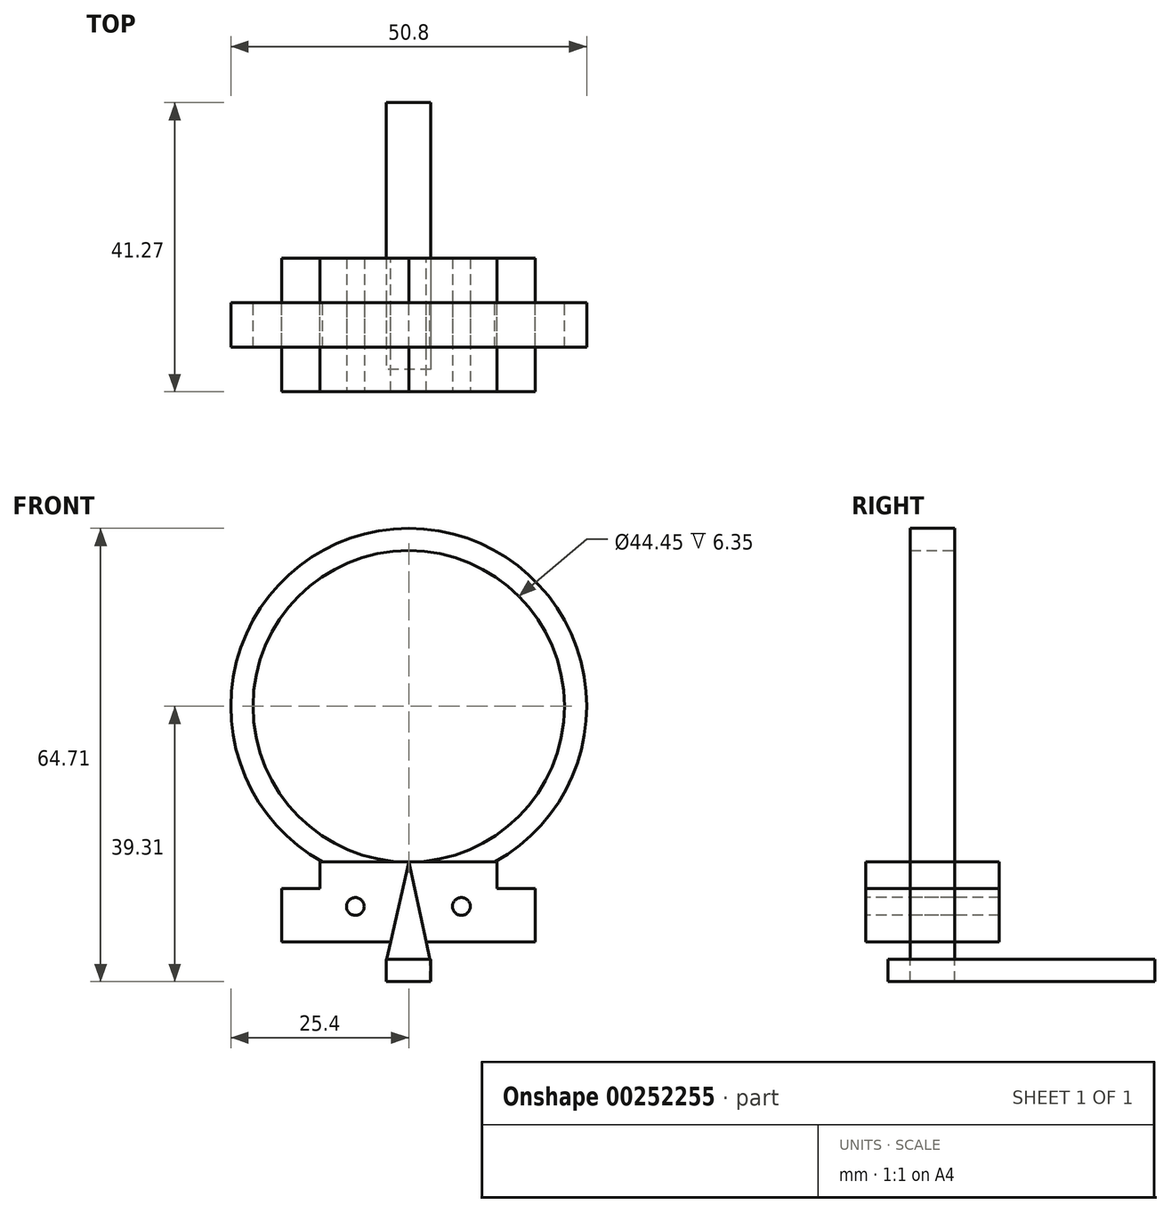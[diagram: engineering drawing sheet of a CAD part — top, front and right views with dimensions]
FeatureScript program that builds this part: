
annotation { "Feature Type Name" : "Feature", "Feature Type Description" : "" }
export const myFeature = defineFeature(function(context is Context, id is Id, definition is map)
    precondition{}
    {
        {
            var Q0;
            Q0=qCreatedBy(makeId("Front.planeOp"),FACE);
            var sketch = newSketch(context, id + "F0", { "sketchPlane" : qUnion([Q0])});
            skArc(sketch, "E0", {"start": v(0, 50.8) * mm, "mid": v(25.36, 26.9) * mm, "end": v(3, 0.18) * mm});
            skArc(sketch, "E1", {"start": v(0, 3.17) * mm, "mid": v(22.23, 25.4) * mm, "end": v(0, 47.63) * mm});
            skFitSpline(sketch, "E2", {"points": [v(0, 50.8) * mm, v(1.45, 49.21) * mm, v(0, 47.63) * mm], "startDerivative": vector(4.36, -3.17) * mm, "endDerivative": vector(-4.36, -3.17) * mm});
            skArc(sketch, "E3", {"start": v(0, 50.8) * mm, "mid": v(-25.36, 26.9) * mm, "end": v(-3, 0.18) * mm});
            skArc(sketch, "E4", {"start": v(0, 47.63) * mm, "mid": v(-22.23, 25.4) * mm, "end": v(0, 3.17) * mm});
            skLineSegment(sketch, "E5", {"start": v(-3, 0.18) * mm, "end": v(0, 3.17) * mm});
            skLineSegment(sketch, "E6", {"start": v(3, 0.18) * mm, "end": v(0, 3.17) * mm});
            skPoint(sketch, "E7.orphan", {"position": v(0, 0) * mm});
            skLineSegment(sketch, "E8", {"start": v(0, 3.17) * mm, "end": v(-12.7, 3.17) * mm});
            skLineSegment(sketch, "E9", {"start": v(-12.7, 3.17) * mm, "end": v(-12.7, -0.64) * mm});
            skLineSegment(sketch, "E10", {"start": v(12.6, -0.64) * mm, "end": v(12.6, 3.17) * mm});
            skLineSegment(sketch, "E11", {"start": v(12.6, 3.17) * mm, "end": v(0, 3.17) * mm});
            skLineSegment(sketch, "E12", {"start": v(-12.7, -0.64) * mm, "end": v(-18.16, -0.64) * mm});
            skLineSegment(sketch, "E13", {"start": v(12.6, -0.64) * mm, "end": v(18.06, -0.64) * mm});
            skLineSegment(sketch, "E14", {"start": v(-18.16, -0.64) * mm, "end": v(-18.16, -8.26) * mm});
            skLineSegment(sketch, "E15", {"start": v(-18.16, -8.26) * mm, "end": v(-2.59, -8.26) * mm});
            skLineSegment(sketch, "E16", {"start": v(18.06, -0.64) * mm, "end": v(18.06, -8.26) * mm});
            skLineSegment(sketch, "E17", {"start": v(2.5, -8.26) * mm, "end": v(0, 3.17) * mm});
            skLineSegment(sketch, "E18", {"start": v(0, 3.17) * mm, "end": v(-2.59, -8.26) * mm});
            skLineSegment(sketch, "E19", {"start": v(-2.59, -8.26) * mm, "end": v(-3.15, -10.73) * mm});
            skLineSegment(sketch, "E20", {"start": v(2.5, -8.26) * mm, "end": v(3.03, -10.74) * mm});
            skLineSegment(sketch, "E21", {"start": v(3.03, -10.74) * mm, "end": v(-3.15, -10.73) * mm});
            skLineSegment(sketch, "E22.trimOffspring", {"start": v(2.5, -8.26) * mm, "end": v(18.06, -8.26) * mm});
            skSolve(sketch);
        }
        {
            var Q0;
            {var subQ4=sQuery(id+"F0.wireOp",EDGE,"E6");Q0=makeQuery(id+"F0.imprint","IMPRINT",FACE,{"disambiguationData":[TD([[makeQuery(id+"F0.imprint","IMPRINT",EDGE,{"derivedFrom":subQ4}),1.0]])]});}
            var Q1;
            {var subQ4=sQuery(id+"F0.wireOp",EDGE,"E5");Q1=makeQuery(id+"F0.imprint","IMPRINT",FACE,{"disambiguationData":[TD([[makeQuery(id+"F0.imprint","IMPRINT",EDGE,{"derivedFrom":subQ4}),-1.0]])]});}
            var Q2;
            {var subQ0=sQuery(id+"F0.wireOp",EDGE,"E6");Q2=makeQuery(id+"F0.imprint","IMPRINT",FACE,{"disambiguationData":[TD([[makeQuery(id+"F0.imprint","IMPRINT",EDGE,{"derivedFrom":subQ0}),-1.0]])]});}
            var Q3;
            {var subQ0=sQuery(id+"F0.wireOp",EDGE,"E5");Q3=makeQuery(id+"F0.imprint","IMPRINT",FACE,{"disambiguationData":[TD([[makeQuery(id+"F0.imprint","IMPRINT",EDGE,{"derivedFrom":subQ0}),1.0]])]});}
            extrude(context, id + "F1", {"entities" : qUnion([Q0, Q1, Q2, Q3]), "depth" : 12.7 * mm});
        }
        {
            var Q0;
            Q0=makeQuery(id+"F1.opExtrude","CAP_FACE",FACE,{"disambiguationData":[OSD([sQuery(id+"F0.wireOp",EDGE,"E0"),sQuery(id+"F0.wireOp",EDGE,"E6"),sQuery(id+"F0.wireOp",EDGE,"E10"),sQuery(id+"F0.wireOp",EDGE,"E11"),sQuery(id+"F0.wireOp",EDGE,"E13"),sQuery(id+"F0.wireOp",EDGE,"E15"),sQuery(id+"F0.wireOp",EDGE,"E16"),sQuery(id+"F0.wireOp",EDGE,"E17")])],"isStart":true});
            var Q1;
            Q1=makeQuery(id+"F1.opExtrude","CAP_FACE",FACE,{"disambiguationData":[OSD([sQuery(id+"F0.wireOp",EDGE,"E3"),sQuery(id+"F0.wireOp",EDGE,"E5"),sQuery(id+"F0.wireOp",EDGE,"E8"),sQuery(id+"F0.wireOp",EDGE,"E9"),sQuery(id+"F0.wireOp",EDGE,"E12"),sQuery(id+"F0.wireOp",EDGE,"E14"),sQuery(id+"F0.wireOp",EDGE,"E15"),sQuery(id+"F0.wireOp",EDGE,"E18")])],"isStart":true});
            extrude(context, id + "F2", {"entities" : qUnion([Q0, Q1]), "operationType" : NewBodyOperationType.ADD, "depth" : 6.35 * mm});
        }
        {
            var Q0;
            Q0 = qSketchRegion(id + "F0", true);
            extrude(context, id + "F3", {"entities" : qUnion([Q0]), "depth" : 6.35 * mm});
        }
        {
            var Q0;
            Q0=makeQuery(id+"F3.opExtrude","SWEPT_FACE",FACE,{"disambiguationData":[OSD([sQuery(id+"F0.wireOp",EDGE,"E21")])]});
            var sketch = newSketch(context, id + "F4", { "sketchPlane" : qUnion([Q0])});
            skLineSegment(sketch, "E23", {"start": v(0, 0) * mm, "end": v(0, 6.35) * mm});
            skLineSegment(sketch, "E24.top", {"start": v(3.18, 9.53) * mm, "end": v(-3.17, 9.53) * mm});
            skLineSegment(sketch, "E24.left", {"start": v(3.18, -3.18) * mm, "end": v(3.18, 9.53) * mm});
            skLineSegment(sketch, "E24.right", {"start": v(-3.18, -3.18) * mm, "end": v(-3.17, 9.53) * mm});
            skPoint(sketch, "E24.middle", {"position": v(0, 3.18) * mm});
            skLineSegment(sketch, "E25", {"start": v(-3.18, -3.18) * mm, "end": v(-3.18, -28.58) * mm});
            skLineSegment(sketch, "E26", {"start": v(-3.18, -28.58) * mm, "end": v(3.18, -28.58) * mm});
            skLineSegment(sketch, "E27", {"start": v(3.18, -28.58) * mm, "end": v(3.18, -3.18) * mm});
            skSolve(sketch);
        }
        {
            var Q0;
            Q0=makeQuery(id+"F4.imprint","IMPRINT",FACE,{"disambiguationData":[TD([[makeQuery(id+"F4.imprint","IMPRINT",EDGE,{"derivedFrom":sQuery(id+"F4.wireOp",EDGE,"E24.top")}),1.0]])]});
            extrude(context, id + "F5", {"entities" : qUnion([Q0]), "operationType" : NewBodyOperationType.ADD, "depth" : 3.17 * mm});
        }
        {
            var Q0;
            Q0=makeQuery(id+"F1.opExtrude","CAP_FACE",FACE,{"disambiguationData":[OSD([sQuery(id+"F0.wireOp",EDGE,"E8"),sQuery(id+"F0.wireOp",EDGE,"E9"),sQuery(id+"F0.wireOp",EDGE,"E12"),sQuery(id+"F0.wireOp",EDGE,"E14"),sQuery(id+"F0.wireOp",EDGE,"E15"),sQuery(id+"F0.wireOp",EDGE,"E18")])],"isStart":false});
            var sketch = newSketch(context, id + "F6", { "sketchPlane" : qUnion([Q0])});
            skCircle(sketch, "E28", {"center": v(-7.62, -3.18) * mm, "radius": 1.27 * mm});
            skSolve(sketch);
        }
        {
            var Q0;
            Q0=makeQuery(id+"F1.opExtrude","CAP_FACE",FACE,{"disambiguationData":[OSD([sQuery(id+"F0.wireOp",EDGE,"E10"),sQuery(id+"F0.wireOp",EDGE,"E11"),sQuery(id+"F0.wireOp",EDGE,"E13"),sQuery(id+"F0.wireOp",EDGE,"E16"),sQuery(id+"F0.wireOp",EDGE,"E17"),sQuery(id+"F0.wireOp",EDGE,"E22.trimOffspring")])],"isStart":false});
            var sketch = newSketch(context, id + "F7", { "sketchPlane" : qUnion([Q0])});
            skCircle(sketch, "E29", {"center": v(7.52, -3.18) * mm, "radius": 1.27 * mm});
            skSolve(sketch);
        }
        {
            var Q0;
            Q0=sQuery(id+"F6.wireOp",VERTEX,"E28.center");
            var Q1;
            Q1=makeQuery(id+"F1.opExtrude","SWEPT_BODY",BODY,{"disambiguationData":[OSD([sQuery(id+"F0.wireOp",EDGE,"E8"),sQuery(id+"F0.wireOp",EDGE,"E9"),sQuery(id+"F0.wireOp",EDGE,"E12"),sQuery(id+"F0.wireOp",EDGE,"E14"),sQuery(id+"F0.wireOp",EDGE,"E15"),sQuery(id+"F0.wireOp",EDGE,"E18")])]});
            var Q2;
            Q2=makeQuery(id+"F3.opExtrude","SWEPT_BODY",BODY,{"disambiguationData":[OSD([sQuery(id+"F0.wireOp",EDGE,"E0"),sQuery(id+"F0.wireOp",EDGE,"E1"),sQuery(id+"F0.wireOp",EDGE,"E3"),sQuery(id+"F0.wireOp",EDGE,"E4"),sQuery(id+"F0.wireOp",EDGE,"E8"),sQuery(id+"F0.wireOp",EDGE,"E9"),sQuery(id+"F0.wireOp",EDGE,"E10"),sQuery(id+"F0.wireOp",EDGE,"E11"),sQuery(id+"F0.wireOp",EDGE,"E12"),sQuery(id+"F0.wireOp",EDGE,"E13"),sQuery(id+"F0.wireOp",EDGE,"E14"),sQuery(id+"F0.wireOp",EDGE,"E15"),sQuery(id+"F0.wireOp",EDGE,"E16"),sQuery(id+"F0.wireOp",EDGE,"E19"),sQuery(id+"F0.wireOp",EDGE,"E20"),sQuery(id+"F0.wireOp",EDGE,"E21"),sQuery(id+"F0.wireOp",EDGE,"E22.trimOffspring")])]});
            hole(context, id + "F8", {"style" : HoleStyle.SIMPLE, "endStyle" : HoleEndStyle.BLIND, "holeDiameter" : 2.54 * mm, "holeDepth" : 25.4 * mm, "tappedDepth" : 12.7 * mm, "tapClearance" : 3, "startFromSketch" : true, "locations" : qUnion([Q0]), "scope" : qUnion([Q1, Q2])});
        }
        {
            var Q0;
            Q0=sQuery(id+"F7.wireOp",VERTEX,"E29.center");
            var Q1;
            {var subQ0=sQuery(id+"F0.wireOp",EDGE,"E22.trimOffspring");var subQ1=sQuery(id+"F0.wireOp",EDGE,"E17");var subQ2=sQuery(id+"F0.wireOp",EDGE,"E16");var subQ3=sQuery(id+"F0.wireOp",EDGE,"E13");var subQ4=sQuery(id+"F0.wireOp",EDGE,"E11");var subQ5=sQuery(id+"F0.wireOp",EDGE,"E10");var subQ6=sQuery(id+"F0.wireOp",EDGE,"E18");var subQ7=sQuery(id+"F0.wireOp",EDGE,"E15");var subQ8=sQuery(id+"F0.wireOp",EDGE,"E14");var subQ9=sQuery(id+"F0.wireOp",EDGE,"E12");var subQ10=sQuery(id+"F0.wireOp",EDGE,"E9");var subQ11=sQuery(id+"F0.wireOp",EDGE,"E8");Q1=makeQuery(id+"F2.boolean.opBoolean","MERGE",BODY,{"derivedFrom":[makeQuery(id+"F1.opExtrude","SWEPT_BODY",BODY,{"disambiguationData":[OSD([subQ11,subQ10,subQ9,subQ8,subQ7,subQ6])]}),makeQuery(id+"F1.opExtrude","SWEPT_BODY",BODY,{"disambiguationData":[OSD([subQ5,subQ4,subQ3,subQ2,subQ1,subQ0])]}),makeQuery(id+"F2.opExtrude","SWEPT_BODY",BODY,{"disambiguationData":[OSD([subQ11,subQ10,subQ9,subQ8,subQ7,subQ6])]}),makeQuery(id+"F2.opExtrude","SWEPT_BODY",BODY,{"disambiguationData":[OSD([subQ5,subQ4,subQ3,subQ2,subQ1,subQ0])]})]});}
            var Q2;
            Q2=makeQuery(id+"F3.opExtrude","SWEPT_BODY",BODY,{"disambiguationData":[OSD([sQuery(id+"F0.wireOp",EDGE,"E0"),sQuery(id+"F0.wireOp",EDGE,"E1"),sQuery(id+"F0.wireOp",EDGE,"E3"),sQuery(id+"F0.wireOp",EDGE,"E4"),sQuery(id+"F0.wireOp",EDGE,"E8"),sQuery(id+"F0.wireOp",EDGE,"E9"),sQuery(id+"F0.wireOp",EDGE,"E10"),sQuery(id+"F0.wireOp",EDGE,"E11"),sQuery(id+"F0.wireOp",EDGE,"E12"),sQuery(id+"F0.wireOp",EDGE,"E13"),sQuery(id+"F0.wireOp",EDGE,"E14"),sQuery(id+"F0.wireOp",EDGE,"E15"),sQuery(id+"F0.wireOp",EDGE,"E16"),sQuery(id+"F0.wireOp",EDGE,"E19"),sQuery(id+"F0.wireOp",EDGE,"E20"),sQuery(id+"F0.wireOp",EDGE,"E21"),sQuery(id+"F0.wireOp",EDGE,"E22.trimOffspring")])]});
            hole(context, id + "F9", {"style" : HoleStyle.SIMPLE, "endStyle" : HoleEndStyle.BLIND, "holeDiameter" : 2.54 * mm, "holeDepth" : 25.4 * mm, "tappedDepth" : 12.7 * mm, "tapClearance" : 3, "startFromSketch" : true, "locations" : qUnion([Q0]), "scope" : qUnion([Q1, Q2])});
        }
    });
